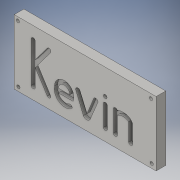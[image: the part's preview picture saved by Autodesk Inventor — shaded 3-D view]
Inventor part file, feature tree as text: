
AUTODESK INVENTOR PART (.ipt)
format: ipt  version: 2016 (Build 200138000, 138)  size: 177,152 bytes
history: native  units: in
note: dims shown in document units (in); Inventor stores cm internally (conversion verified against a paired STEP export)
features: hole x4, sketch x2, extrude x1, emboss x1
ambient origin geometry x8: Origin, YZ Plane, XZ Plane, XY Plane, X Axis, Y Axis, Z Axis, Center Point
bodies: Solid1 (feature_tree)
feature tree (8):
  extrude  "Extrusion1"  Depth=11.0in
  emboss  "Emboss1"
  hole  "Hole1"  [1 undecoded]
  hole  "Hole2"  [1 undecoded]
  hole  "Hole3"  [1 undecoded]
  hole  "Hole4"  [1 undecoded]
  sketch  "Sketch1"  dims[d0=5.0in d1=11.0in]
  sketch  "Sketch2"  dims[d2=0.75in d3=0.0in d4=0.25in d5=0.0in d6=1.0in d7=1.0in d8=0.25in d9=0.75in d10=0.375in d11=0.25in d12=0.5635in d13=1.0in d14=0.8108in d15=1.0in d16=1.0in d17=0.25in d18=0.75in d19=0.375in d20=0.25in d21=0.5635in d22=1.0in d23=0.8108in d24=1.0in d25=1.0in d26=0.25in d27=0.75in d28=0.375in d29=0.25in d30=0.5635in d31=1.0in d32=0.8108in d33=1.0in d34=1.0in d35=0.25in d36=0.75in d37=0.375in d38=0.25in d39=0.5635in d40=1.0in d41=0.8108in]
note: 4 required parameter values undecoded (feature->parameter linkage not recoverable at this tier; creation-order binding heuristic only, values carry confidence <= 0.55)
